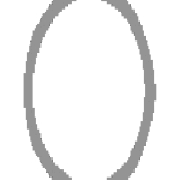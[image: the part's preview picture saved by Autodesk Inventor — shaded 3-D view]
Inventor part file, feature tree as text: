
AUTODESK INVENTOR PART (.ipt)
format: ipt  version: 2021 (Build 250183000, 183)  size: 112,128 bytes
history: native  units: in
note: dims shown in document units (in); Inventor stores cm internally (conversion verified against a paired STEP export)
features: other x4, sketch x3, plane x1
ambient origin geometry x8: Origin, YZ Plane, XZ Plane, XY Plane, X Axis, Y Axis, Z Axis, Center Point
bodies: Solid1 (feature_tree), Body (feature_tree)
feature tree (8):
  other  "Driven Length"
  other  "Frame Generator"
  other  "Start Plane"
  other  "End Plane"
  sketch  "Sketch"  dims[d2=16.0833in d4=-0.0in d5=16.0833in d6=0.12in d7=0.0in d8=90.0deg d9=16.0833in]
  sketch  "Sketch2"  dims[d0=1.0in]
  plane  "Work Plane3"
  sketch  "Sketch3"  dims[d1=0.065in]
